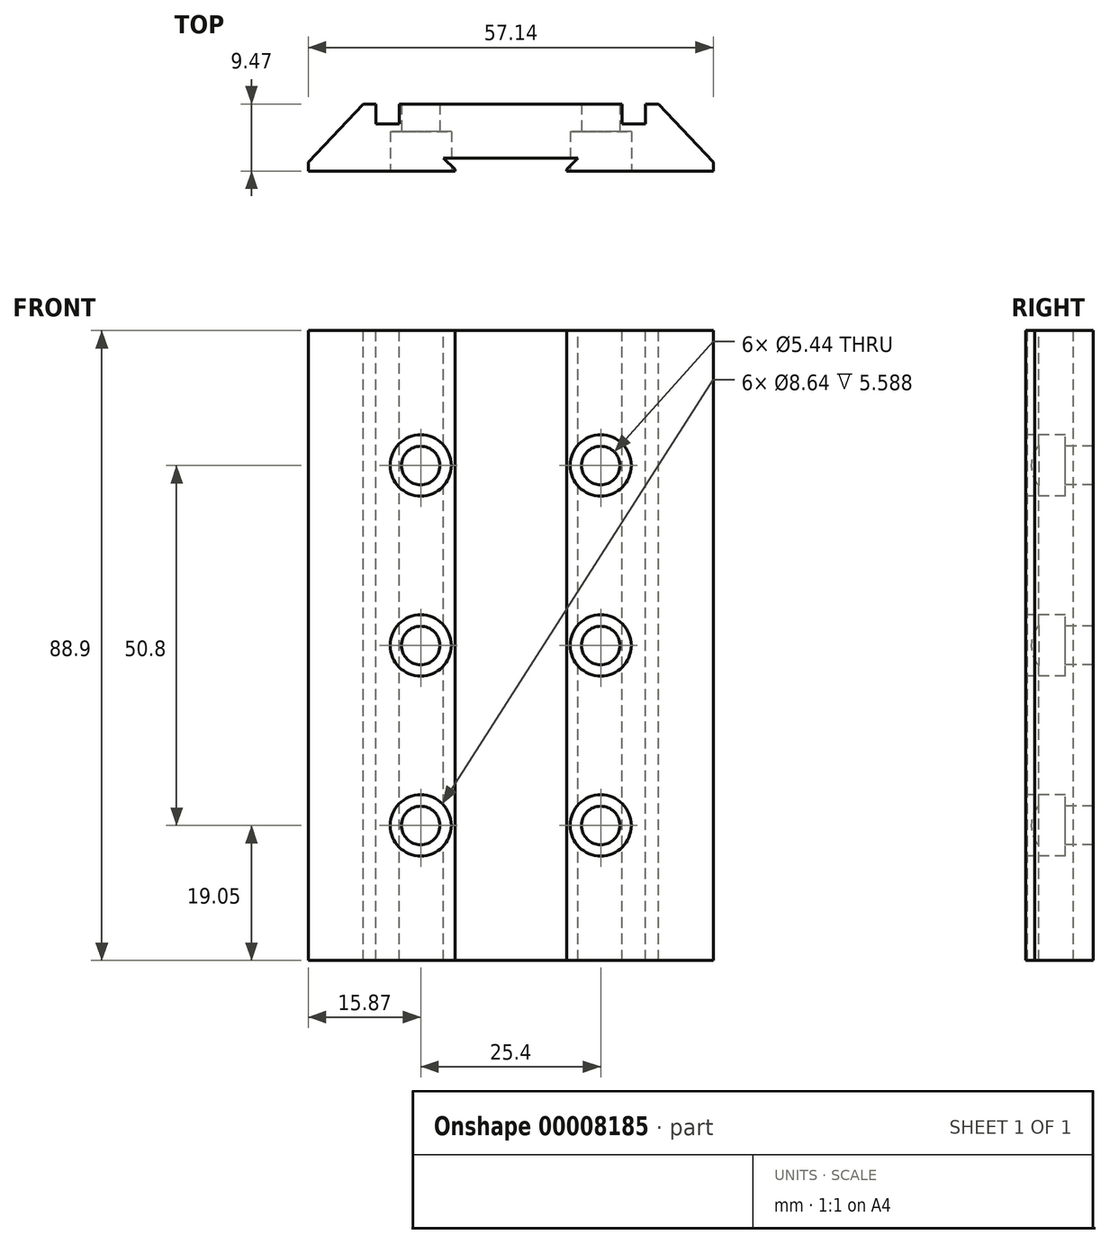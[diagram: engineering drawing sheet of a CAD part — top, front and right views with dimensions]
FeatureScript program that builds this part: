
annotation { "Feature Type Name" : "Feature", "Feature Type Description" : "" }
export const myFeature = defineFeature(function(context is Context, id is Id, definition is map)
    precondition{}
    {
        {
            var Q0;
            Q0=qCreatedBy(makeId("Top.planeOp"),FACE);
            var sketch = newSketch(context, id + "F0", { "sketchPlane" : qUnion([Q0])});
            skLineSegment(sketch, "E0", {"start": v(-53, 0) * mm, "end": v(54.1, 0) * mm, "construction": true});
            skLineSegment(sketch, "E1", {"start": v(-28.58, 0) * mm, "end": v(-7.87, 0) * mm});
            skLineSegment(sketch, "E2", {"start": v(-7.87, 0) * mm, "end": v(-7.87, 0.25) * mm});
            skLineSegment(sketch, "E3", {"start": v(-7.87, 0.25) * mm, "end": v(-9.47, 1.85) * mm});
            skLineSegment(sketch, "E4", {"start": v(-9.47, 1.85) * mm, "end": v(9.47, 1.85) * mm});
            skLineSegment(sketch, "E5", {"start": v(9.47, 1.85) * mm, "end": v(7.87, 0.25) * mm});
            skLineSegment(sketch, "E6", {"start": v(7.87, 0.25) * mm, "end": v(7.87, 0) * mm});
            skLineSegment(sketch, "E7", {"start": v(7.87, 0) * mm, "end": v(28.58, 0) * mm});
            skLineSegment(sketch, "E8", {"start": v(28.58, 0) * mm, "end": v(28.58, 1.27) * mm});
            skLineSegment(sketch, "E9", {"start": v(28.58, 1.27) * mm, "end": v(20.83, 9.47) * mm});
            skLineSegment(sketch, "E10", {"start": v(20.83, 9.47) * mm, "end": v(19, 9.47) * mm});
            skLineSegment(sketch, "E11", {"start": v(19, 9.47) * mm, "end": v(19, 6.68) * mm});
            skLineSegment(sketch, "E12", {"start": v(19, 6.68) * mm, "end": v(15.7, 6.68) * mm});
            skLineSegment(sketch, "E13", {"start": v(15.7, 6.68) * mm, "end": v(15.7, 9.47) * mm});
            skLineSegment(sketch, "E14", {"start": v(15.7, 9.47) * mm, "end": v(-15.7, 9.47) * mm});
            skLineSegment(sketch, "E15", {"start": v(-15.7, 9.47) * mm, "end": v(-15.7, 6.68) * mm});
            skLineSegment(sketch, "E16", {"start": v(-15.7, 6.68) * mm, "end": v(-19, 6.68) * mm});
            skLineSegment(sketch, "E17", {"start": v(-19, 6.68) * mm, "end": v(-19, 9.47) * mm});
            skLineSegment(sketch, "E18", {"start": v(-19, 9.47) * mm, "end": v(-20.83, 9.47) * mm});
            skLineSegment(sketch, "E19", {"start": v(-20.83, 9.47) * mm, "end": v(-28.58, 1.27) * mm});
            skLineSegment(sketch, "E20", {"start": v(-28.58, 1.27) * mm, "end": v(-28.58, 0) * mm});
            skPoint(sketch, "E21", {"position": v(0, 0) * mm});
            skSolve(sketch);
        }
        {
            var Q0;
            Q0 = qSketchRegion(id + "F0", true);
            extrude(context, id + "F1", {"entities" : qUnion([Q0]), "oppositeDirection" : true, "depth" : 88.9 * mm});
        }
        {
            var Q0;
            Q0=makeQuery(id+"F1.opExtrude","SWEPT_FACE",FACE,{"disambiguationData":[OSD([sQuery(id+"F0.wireOp",EDGE,"E1")])]});
            var sketch = newSketch(context, id + "F2", { "sketchPlane" : qUnion([Q0])});
            skLineSegment(sketch, "E22", {"start": v(-12.7, 12.49) * mm, "end": v(-12.7, -91.72) * mm, "construction": true});
            skLineSegment(sketch, "E23", {"start": v(12.7, 12.87) * mm, "end": v(12.7, -92.1) * mm, "construction": true});
            skLineSegment(sketch, "E24", {"start": v(-38.96, -14.73) * mm, "end": v(43.72, -14.73) * mm, "construction": true});
            skLineSegment(sketch, "E25", {"start": v(-38.96, -16.33) * mm, "end": v(43.72, -16.33) * mm, "construction": true});
            skLineSegment(sketch, "E26", {"start": v(-39.34, -21.77) * mm, "end": v(43.34, -21.77) * mm, "construction": true});
            skLineSegment(sketch, "E27", {"start": v(-39.34, -23.37) * mm, "end": v(43.34, -23.37) * mm, "construction": true});
            skLineSegment(sketch, "E28", {"start": v(-39.34, -40.13) * mm, "end": v(43.34, -40.13) * mm, "construction": true});
            skLineSegment(sketch, "E29", {"start": v(-39.34, -65.53) * mm, "end": v(43.34, -65.53) * mm, "construction": true});
            skCircle(sketch, "E30", {"center": v(-12.7, -19.05) * mm, "radius": 2.72 * mm});
            skCircle(sketch, "E31", {"center": v(12.7, -19.05) * mm, "radius": 2.72 * mm});
            skCircle(sketch, "E32", {"center": v(-12.7, -44.45) * mm, "radius": 2.72 * mm});
            skCircle(sketch, "E33", {"center": v(12.7, -44.45) * mm, "radius": 2.72 * mm});
            skCircle(sketch, "E34", {"center": v(-12.7, -69.85) * mm, "radius": 2.72 * mm});
            skCircle(sketch, "E35", {"center": v(12.7, -69.85) * mm, "radius": 2.72 * mm});
            skCircle(sketch, "E36", {"center": v(-12.7, -19.05) * mm, "radius": 4.32 * mm});
            skCircle(sketch, "E37", {"center": v(12.7, -19.05) * mm, "radius": 4.32 * mm});
            skCircle(sketch, "E38", {"center": v(-12.7, -44.45) * mm, "radius": 4.32 * mm});
            skCircle(sketch, "E39", {"center": v(12.7, -44.45) * mm, "radius": 4.32 * mm});
            skCircle(sketch, "E40", {"center": v(-12.7, -69.85) * mm, "radius": 4.32 * mm});
            skCircle(sketch, "E41", {"center": v(12.7, -69.85) * mm, "radius": 4.32 * mm});
            skSolve(sketch);
        }
        {
            var Q0;
            Q0=makeQuery(id+"F2.imprint","IMPRINT",FACE,{"disambiguationData":[TD([[makeQuery(id+"F2.imprint","IMPRINT",EDGE,{"derivedFrom":sQuery(id+"F2.wireOp",EDGE,"E30")}),1.0]])]});
            var Q1;
            Q1=makeQuery(id+"F2.imprint","IMPRINT",FACE,{"disambiguationData":[TD([[makeQuery(id+"F2.imprint","IMPRINT",EDGE,{"derivedFrom":sQuery(id+"F2.wireOp",EDGE,"E31")}),1.0]])]});
            var Q2;
            Q2=makeQuery(id+"F2.imprint","IMPRINT",FACE,{"disambiguationData":[TD([[makeQuery(id+"F2.imprint","IMPRINT",EDGE,{"derivedFrom":sQuery(id+"F2.wireOp",EDGE,"E32")}),1.0]])]});
            var Q3;
            Q3=makeQuery(id+"F2.imprint","IMPRINT",FACE,{"disambiguationData":[TD([[makeQuery(id+"F2.imprint","IMPRINT",EDGE,{"derivedFrom":sQuery(id+"F2.wireOp",EDGE,"E33")}),1.0]])]});
            var Q4;
            Q4=makeQuery(id+"F2.imprint","IMPRINT",FACE,{"disambiguationData":[TD([[makeQuery(id+"F2.imprint","IMPRINT",EDGE,{"derivedFrom":sQuery(id+"F2.wireOp",EDGE,"E35")}),1.0]])]});
            var Q5;
            Q5=makeQuery(id+"F2.imprint","IMPRINT",FACE,{"disambiguationData":[TD([[makeQuery(id+"F2.imprint","IMPRINT",EDGE,{"derivedFrom":sQuery(id+"F2.wireOp",EDGE,"E34")}),1.0]])]});
            var Q6;
            Q6=makeQuery(id+"F1.opExtrude","SWEPT_FACE",FACE,{"disambiguationData":[OSD([sQuery(id+"F0.wireOp",EDGE,"E14")])]});
            extrude(context, id + "F3", {"entities" : qUnion([Q0, Q1, Q2, Q3, Q4, Q5]), "operationType" : NewBodyOperationType.REMOVE, "endBound" : BoundingType.UP_TO_SURFACE, "oppositeDirection" : true, "endBoundEntityFace" : qUnion([Q6]), "depth" : 25.4 * mm});
        }
        {
            var Q0;
            Q0 = qSketchRegion(id + "F2", true);
            extrude(context, id + "F4", {"entities" : qUnion([Q0]), "operationType" : NewBodyOperationType.REMOVE, "oppositeDirection" : true, "depth" : 5.6 * mm});
        }
    });
